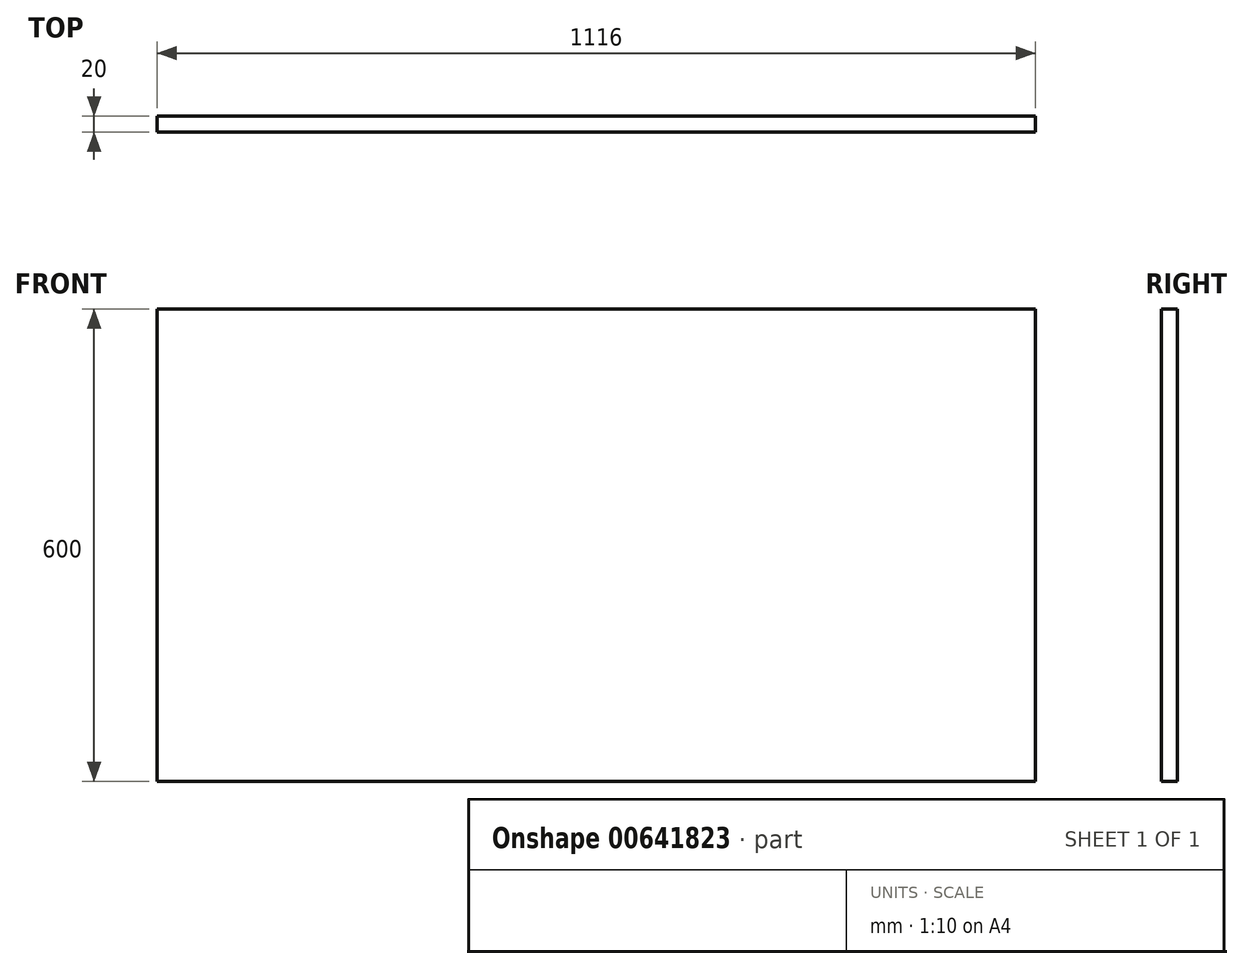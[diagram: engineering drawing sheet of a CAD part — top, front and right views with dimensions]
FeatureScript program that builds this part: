
annotation { "Feature Type Name" : "Feature", "Feature Type Description" : "" }
export const myFeature = defineFeature(function(context is Context, id is Id, definition is map)
    precondition{}
    {
        {
            var Q0;
            Q0=qCreatedBy(makeId("Front.planeOp"),FACE);
            var sketch = newSketch(context, id + "F0", { "sketchPlane" : qUnion([Q0])});
            skLineSegment(sketch, "E0.bottom", {"start": v(-109.86, 594.1) * mm, "end": v(1006.14, 594.1) * mm});
            skLineSegment(sketch, "E0.top", {"start": v(-109.86, -5.9) * mm, "end": v(1006.14, -5.9) * mm});
            skLineSegment(sketch, "E0.left", {"start": v(-109.86, 594.1) * mm, "end": v(-109.86, -5.9) * mm});
            skLineSegment(sketch, "E0.right", {"start": v(1006.14, 594.1) * mm, "end": v(1006.14, -5.9) * mm});
            skSolve(sketch);
        }
        {
            var Q0;
            Q0=makeQuery(id+"F0.imprint","IMPRINT",FACE,{"disambiguationData":[TD([[makeQuery(id+"F0.imprint","IMPRINT",EDGE,{"derivedFrom":sQuery(id+"F0.wireOp",EDGE,"E0.bottom")}),-1.0]])]});
            extrude(context, id + "F1", {"entities" : qUnion([Q0]), "depth" : 20 * mm, "offsetDistance" : 25 * mm});
        }
    });
